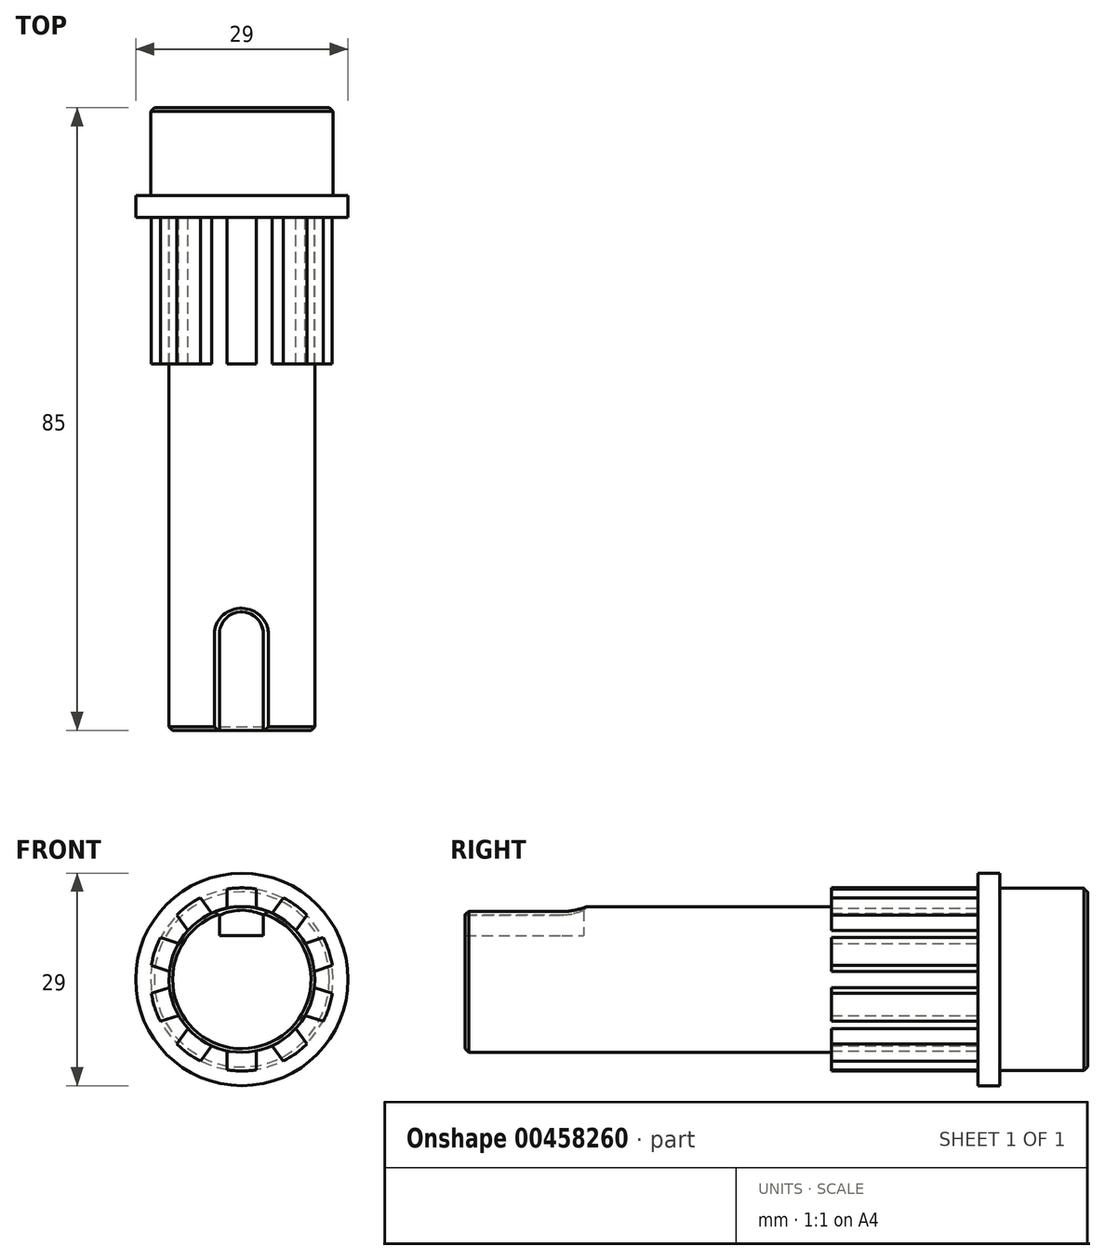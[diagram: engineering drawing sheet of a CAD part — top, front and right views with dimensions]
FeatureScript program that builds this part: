
annotation { "Feature Type Name" : "Feature", "Feature Type Description" : "" }
export const myFeature = defineFeature(function(context is Context, id is Id, definition is map)
    precondition{}
    {
        {
            var Q0;
            Q0=qCreatedBy(makeId("Front.planeOp"),FACE);
            var sketch = newSketch(context, id + "F0", { "sketchPlane" : qUnion([Q0])});
            skCircle(sketch, "E0", {"center": v(0, 0) * mm, "radius": 14.5 * mm});
            skSolve(sketch);
        }
        {
            var Q0;
            Q0=makeQuery(id+"F0.imprint","IMPRINT",FACE,{"disambiguationData":[TD([[makeQuery(id+"F0.imprint","IMPRINT",EDGE,{"derivedFrom":sQuery(id+"F0.wireOp",EDGE,"E0")}),1.0]])]});
            extrude(context, id + "F1", {"entities" : qUnion([Q0]), "oppositeDirection" : true, "depth" : 3 * mm});
        }
        {
            var Q0;
            Q0=qCreatedBy(makeId("Front.planeOp"),FACE);
            var sketch = newSketch(context, id + "F2", { "sketchPlane" : qUnion([Q0])});
            skCircle(sketch, "E1", {"center": v(0, 0) * mm, "radius": 9.95 * mm});
            skSolve(sketch);
        }
        {
            var Q0;
            Q0 = qSketchRegion(id + "F2", true);
            extrude(context, id + "F3", {"entities" : qUnion([Q0]), "operationType" : NewBodyOperationType.ADD, "depth" : 70 * mm});
        }
        {
            var Q0;
            Q0=makeQuery(id+"F1.opExtrude","CAP_FACE",FACE,{"disambiguationData":[OSD([sQuery(id+"F0.wireOp",EDGE,"E0")])],"isStart":false});
            cPlane(context, id + "F4", {"entities" : qUnion([Q0]), "cplaneType" : CPlaneType.OFFSET, "offset" : 0 * mm, "width" : 150 * mm, "height" : 150 * mm});
        }
        {
            var Q0;
            Q0=qCreatedBy(id+"F4.planeOp",FACE);
            var sketch = newSketch(context, id + "F5", { "sketchPlane" : qUnion([Q0])});
            skCircle(sketch, "E2", {"center": v(0, 0) * mm, "radius": 12.45 * mm});
            skSolve(sketch);
        }
        {
            var Q0;
            Q0 = qSketchRegion(id + "F5", true);
            extrude(context, id + "F6", {"entities" : qUnion([Q0]), "operationType" : NewBodyOperationType.ADD, "depth" : 12 * mm});
        }
        {
            var Q0;
            Q0=makeQuery(id+"F1.opExtrude","CAP_FACE",FACE,{"disambiguationData":[OSD([sQuery(id+"F0.wireOp",EDGE,"E0")])],"isStart":true});
            var sketch = newSketch(context, id + "F7", { "sketchPlane" : qUnion([Q0])});
            skLineSegment(sketch, "E3.left", {"start": v(-2, 12.34) * mm, "end": v(-2, 6.95) * mm});
            skLineSegment(sketch, "E3.right", {"start": v(2, 12.34) * mm, "end": v(2, 6.95) * mm});
            skPoint(sketch, "E3.middle", {"position": v(0, 9.95) * mm});
            skCircle(sketch, "E4", {"center": v(0, 0) * mm, "radius": 12.5 * mm});
            skPoint(sketch, "E3.bottom.end.orphan", {"position": v(2, 12.95) * mm});
            skPoint(sketch, "E3.bottom.start.orphan", {"position": v(-2, 12.95) * mm});
            skSolve(sketch);
        }
        {
            var Q0;
            {var subQ0=sQuery(id+"F7.wireOp",EDGE,"E4");var subQ1=sQuery(id+"F7.wireOp",EDGE,"E3.left");var subQ2=makeQuery(id+"F7.imprint","INTERSECT",VERTEX,{"derivedFrom":[subQ1,subQ0]});Q0=makeQuery(id+"F7.imprint","IMPRINT",FACE,{"disambiguationData":[TD([[makeQuery(id+"F7.imprint","IMPRINT",EDGE,{"disambiguationData":[TD([[subQ2,-1.0]])],"derivedFrom":subQ1}),1.0]])]});}
            extrude(context, id + "F8", {"entities" : qUnion([Q0]), "operationType" : NewBodyOperationType.ADD, "depth" : 20 * mm, "offsetDistance" : 25 * mm});
        }
        {
            var Q0;
            Q0=qCreatedBy(makeId("Right.planeOp"),FACE);
            var sketch = newSketch(context, id + "F9", { "sketchPlane" : qUnion([Q0])});
            skLineSegment(sketch, "E5", {"start": v(-94.35, 0) * mm, "end": v(57.3, 0) * mm, "construction": true});
            skSolve(sketch);
        }
        {
            var Q0;
            Q0=makeQuery(id+"F1.opExtrude","SWEPT_BODY",BODY,{"disambiguationData":[OSD([sQuery(id+"F0.wireOp",EDGE,"E0")])]});
            var Q1;
            Q1=sQuery(id+"F9.wireOp",EDGE,"E5");
            circularPattern(context, id + "F10", {"operationType" : NewBodyOperationType.ADD, "entities" : qUnion([Q0]), "axis" : qUnion([Q1]), "angle" : 360 * degree, "instanceCount" : 10, "equalSpace" : true});
        }
        {
            var Q0;
            Q0=makeQuery(id+"F3.opExtrude","CAP_EDGE",EDGE,{"disambiguationData":[OSD([sQuery(id+"F2.wireOp",EDGE,"E1")])],"isStart":false});
            chamfer(context, id + "F11", {"entities" : qUnion([Q0]), "width" : 0.5 * mm, "tangentPropagation" : true});
        }
        {
            var Q0;
            Q0=qCreatedBy(makeId("Top.planeOp"),FACE);
            cPlane(context, id + "F12", {"entities" : qUnion([Q0]), "cplaneType" : CPlaneType.OFFSET, "offset" : 6 * mm, "width" : 150 * mm, "height" : 150 * mm});
        }
        {
            var Q0;
            Q0=qCreatedBy(id+"F12.planeOp",FACE);
            var sketch = newSketch(context, id + "F13", { "sketchPlane" : qUnion([Q0])});
            skLineSegment(sketch, "E6.bottom", {"start": v(-3.06, -70) * mm, "end": v(2.94, -70) * mm});
            skLineSegment(sketch, "E6.top", {"start": v(-3.06, -56.83) * mm, "end": v(2.94, -56.83) * mm});
            skLineSegment(sketch, "E6.left", {"start": v(-3.06, -70) * mm, "end": v(-3.06, -56.83) * mm});
            skLineSegment(sketch, "E6.right", {"start": v(2.94, -70) * mm, "end": v(2.94, -56.83) * mm});
            skArc(sketch, "E7", {"start": v(-3.06, -56.83) * mm, "mid": v(-0.06, -53.83) * mm, "end": v(2.94, -56.83) * mm});
            skSolve(sketch);
        }
        {
            var Q0;
            Q0 = qSketchRegion(id + "F13", true);
            extrude(context, id + "F14", {"entities" : qUnion([Q0]), "operationType" : NewBodyOperationType.REMOVE, "depth" : 25 * mm});
        }
        {
            var Q0;
            Q0=makeQuery(id+"F14.boolean.opBoolean","INTERSECT",EDGE,{"derivedFrom":[makeQuery(id+"F3.opExtrude","SWEPT_FACE",FACE,{"disambiguationData":[OSD([sQuery(id+"F2.wireOp",EDGE,"E1")])]}),makeQuery(id+"F14.opExtrude","SWEPT_FACE",FACE,{"disambiguationData":[OSD([sQuery(id+"F13.wireOp",EDGE,"E6.left")])]})]});
            var Q1;
            Q1=makeQuery(id+"F14.boolean.opBoolean","INTERSECT",EDGE,{"derivedFrom":[makeQuery(id+"F3.opExtrude","SWEPT_FACE",FACE,{"disambiguationData":[OSD([sQuery(id+"F2.wireOp",EDGE,"E1")])]}),makeQuery(id+"F14.opExtrude","SWEPT_FACE",FACE,{"disambiguationData":[OSD([sQuery(id+"F13.wireOp",EDGE,"E7")])]})]});
            var Q2;
            Q2=makeQuery(id+"F14.boolean.opBoolean","INTERSECT",EDGE,{"derivedFrom":[makeQuery(id+"F3.opExtrude","SWEPT_FACE",FACE,{"disambiguationData":[OSD([sQuery(id+"F2.wireOp",EDGE,"E1")])]}),makeQuery(id+"F14.opExtrude","SWEPT_FACE",FACE,{"disambiguationData":[OSD([sQuery(id+"F13.wireOp",EDGE,"E6.right")])]})]});
            chamfer(context, id + "F15", {"entities" : qUnion([Q0, Q1, Q2]), "width" : 0.5 * mm, "tangentPropagation" : true});
        }
        {
            var Q0;
            Q0=makeQuery(id+"F6.opExtrude","CAP_EDGE",EDGE,{"disambiguationData":[OSD([sQuery(id+"F5.wireOp",EDGE,"E2")])],"isStart":false});
            chamfer(context, id + "F16", {"entities" : qUnion([Q0]), "width" : 0.5 * mm, "tangentPropagation" : true});
        }
    });
